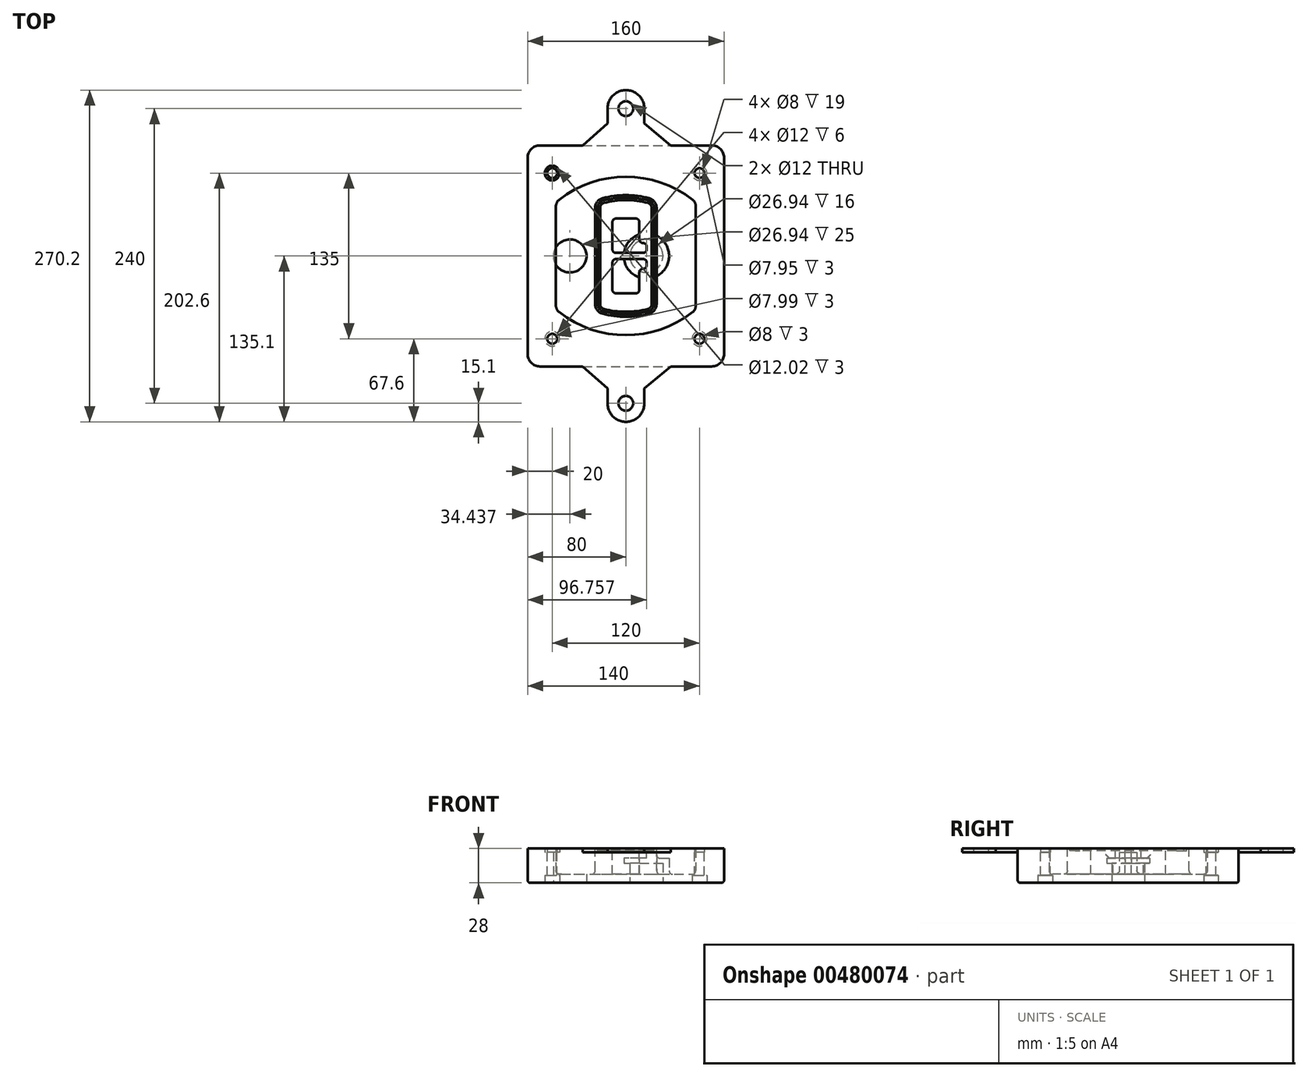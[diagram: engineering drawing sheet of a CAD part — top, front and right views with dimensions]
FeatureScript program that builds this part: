
annotation { "Feature Type Name" : "Feature", "Feature Type Description" : "" }
export const myFeature = defineFeature(function(context is Context, id is Id, definition is map)
    precondition{}
    {
        {
            var Q0;
            Q0=qCreatedBy(makeId("Top.planeOp"),FACE);
            var sketch = newSketch(context, id + "F0", { "sketchPlane" : qUnion([Q0])});
            skPoint(sketch, "E0.rect.middle", {"position": v(0, 0) * mm});
            skLineSegment(sketch, "E1.bottom", {"start": v(-70, -90) * mm, "end": v(70, -90) * mm});
            skLineSegment(sketch, "E1.top", {"start": v(-70, 90) * mm, "end": v(70, 90) * mm});
            skLineSegment(sketch, "E1.left", {"start": v(-80, -80) * mm, "end": v(-80, 80) * mm});
            skLineSegment(sketch, "E1.right", {"start": v(80, -80) * mm, "end": v(80, 80) * mm});
            skLineSegment(sketch, "E2", {"start": v(-80, 90) * mm, "end": v(80, -90) * mm, "construction": true});
            skLineSegment(sketch, "E3", {"start": v(80, 90) * mm, "end": v(-80, -90) * mm, "construction": true});
            skCircle(sketch, "E4", {"center": v(-60, 67.5) * mm, "radius": 4 * mm});
            skCircle(sketch, "E5", {"center": v(60, 67.5) * mm, "radius": 4 * mm});
            skCircle(sketch, "E6", {"center": v(60, -67.5) * mm, "radius": 4 * mm});
            skCircle(sketch, "E7", {"center": v(-60, -67.5) * mm, "radius": 4 * mm});
            skLineSegment(sketch, "E8", {"start": v(-60, 67.5) * mm, "end": v(60, 67.5) * mm, "construction": true});
            skLineSegment(sketch, "E9", {"start": v(60, 67.5) * mm, "end": v(60, -67.5) * mm, "construction": true});
            skLineSegment(sketch, "E10", {"start": v(60, -67.5) * mm, "end": v(-60, -67.5) * mm, "construction": true});
            skLineSegment(sketch, "E11", {"start": v(-60, -67.5) * mm, "end": v(-60, 67.5) * mm, "construction": true});
            skLineSegment(sketch, "E12", {"start": v(-60, 40.3) * mm, "end": v(-60, -40.3) * mm});
            skLineSegment(sketch, "E13", {"start": v(60, 40.3) * mm, "end": v(60, -40.3) * mm});
            skArc(sketch, "E14", {"start": v(56.15, 48.18) * mm, "mid": v(0, 67.5) * mm, "end": v(-56.15, 48.18) * mm});
            skArc(sketch, "E15", {"start": v(-56.15, -48.18) * mm, "mid": v(0, -67.5) * mm, "end": v(56.15, -48.18) * mm});
            skLineSegment(sketch, "E16", {"start": v(-60, 0) * mm, "end": v(60, 0) * mm, "construction": true});
            skPoint(sketch, "E17.visualSharp", {"position": v(-60, -45) * mm});
            skArc(sketch, "E17.filletArc", {"start": v(-60, -40.3) * mm, "mid": v(-58.99, -44.68) * mm, "end": v(-56.15, -48.18) * mm});
            skPoint(sketch, "E18.visualSharp", {"position": v(-60, 45) * mm});
            skArc(sketch, "E18.filletArc", {"start": v(-56.15, 48.18) * mm, "mid": v(-58.99, 44.68) * mm, "end": v(-60, 40.3) * mm});
            skPoint(sketch, "E19.visualSharp", {"position": v(60, 45) * mm});
            skArc(sketch, "E19.filletArc", {"start": v(60, 40.3) * mm, "mid": v(58.99, 44.68) * mm, "end": v(56.15, 48.18) * mm});
            skPoint(sketch, "E20.visualSharp", {"position": v(60, -45) * mm});
            skArc(sketch, "E20.filletArc", {"start": v(56.15, -48.18) * mm, "mid": v(58.99, -44.68) * mm, "end": v(60, -40.3) * mm});
            skPoint(sketch, "E21.visualSharp", {"position": v(-80, 90) * mm});
            skArc(sketch, "E21.filletArc", {"start": v(-70, 90) * mm, "mid": v(-77.07, 87.07) * mm, "end": v(-80, 80) * mm});
            skPoint(sketch, "E22.visualSharp", {"position": v(80, 90) * mm});
            skArc(sketch, "E22.filletArc", {"start": v(80, 80) * mm, "mid": v(77.07, 87.07) * mm, "end": v(70, 90) * mm});
            skPoint(sketch, "E23.visualSharp", {"position": v(80, -90) * mm});
            skArc(sketch, "E23.filletArc", {"start": v(70, -90) * mm, "mid": v(77.07, -87.07) * mm, "end": v(80, -80) * mm});
            skPoint(sketch, "E24.visualSharp", {"position": v(-80, -90) * mm});
            skArc(sketch, "E24.filletArc", {"start": v(-80, -80) * mm, "mid": v(-77.07, -87.07) * mm, "end": v(-70, -90) * mm});
            skArc(sketch, "E25.0", {"start": v(57, 40.3) * mm, "mid": v(56.3, 43.36) * mm, "end": v(54.3, 45.81) * mm});
            skLineSegment(sketch, "E25.1", {"start": v(57, 40.3) * mm, "end": v(57, -40.3) * mm});
            skArc(sketch, "E25.2", {"start": v(54.3, -45.81) * mm, "mid": v(56.3, -43.36) * mm, "end": v(57, -40.3) * mm});
            skArc(sketch, "E25.3", {"start": v(-54.3, -45.81) * mm, "mid": v(0, -64.5) * mm, "end": v(54.3, -45.81) * mm});
            skArc(sketch, "E25.4", {"start": v(-57, -40.3) * mm, "mid": v(-56.3, -43.36) * mm, "end": v(-54.3, -45.81) * mm});
            skArc(sketch, "E25.5", {"start": v(54.3, 45.81) * mm, "mid": v(0, 64.5) * mm, "end": v(-54.3, 45.81) * mm});
            skLineSegment(sketch, "E25.6", {"start": v(-57, 40.3) * mm, "end": v(-57, -40.3) * mm});
            skArc(sketch, "E25.7", {"start": v(-54.3, 45.81) * mm, "mid": v(-56.3, 43.36) * mm, "end": v(-57, 40.3) * mm});
            skArc(sketch, "E26.0", {"start": v(-58.62, 51.33) * mm, "mid": v(-62.58, 46.43) * mm, "end": v(-64, 40.3) * mm});
            skArc(sketch, "E26.1", {"start": v(58.62, 51.33) * mm, "mid": v(0, 71.5) * mm, "end": v(-58.62, 51.33) * mm});
            skArc(sketch, "E26.2", {"start": v(64, 40.3) * mm, "mid": v(62.58, 46.43) * mm, "end": v(58.62, 51.33) * mm});
            skLineSegment(sketch, "E26.3", {"start": v(64, 40.3) * mm, "end": v(64, -40.3) * mm});
            skArc(sketch, "E26.4", {"start": v(58.62, -51.33) * mm, "mid": v(62.58, -46.43) * mm, "end": v(64, -40.3) * mm});
            skLineSegment(sketch, "E26.5", {"start": v(-64, 40.3) * mm, "end": v(-64, -40.3) * mm});
            skArc(sketch, "E26.6", {"start": v(-58.62, -51.33) * mm, "mid": v(0, -71.5) * mm, "end": v(58.62, -51.33) * mm});
            skArc(sketch, "E26.7", {"start": v(-64, -40.3) * mm, "mid": v(-62.58, -46.43) * mm, "end": v(-58.62, -51.33) * mm});
            skSolve(sketch);
        }
        {
            var Q0;
            Q0=makeQuery(id+"F0.imprint","IMPRINT",FACE,{"disambiguationData":[TD([[makeQuery(id+"F0.imprint","IMPRINT",EDGE,{"derivedFrom":sQuery(id+"F0.wireOp",EDGE,"E1.bottom")}),1.0]])]});
            var Q1;
            Q1=makeQuery(id+"F0.imprint","IMPRINT",FACE,{"disambiguationData":[TD([[makeQuery(id+"F0.imprint","IMPRINT",EDGE,{"derivedFrom":sQuery(id+"F0.wireOp",EDGE,"E12")}),1.0]])]});
            var Q2;
            Q2=makeQuery(id+"F0.imprint","IMPRINT",FACE,{"disambiguationData":[TD([[makeQuery(id+"F0.imprint","IMPRINT",EDGE,{"derivedFrom":sQuery(id+"F0.wireOp",EDGE,"E25.0")}),1.0]])]});
            var Q3;
            Q3=makeQuery(id+"F0.imprint","IMPRINT",FACE,{"disambiguationData":[TD([[makeQuery(id+"F0.imprint","IMPRINT",EDGE,{"derivedFrom":sQuery(id+"F0.wireOp",EDGE,"E12")}),-1.0]])]});
            extrude(context, id + "F1", {"entities" : qUnion([Q0, Q1, Q2, Q3]), "oppositeDirection" : true, "depth" : 25 * mm});
        }
        {
            var Q0;
            Q0=makeQuery(id+"F0.imprint","IMPRINT",FACE,{"disambiguationData":[TD([[makeQuery(id+"F0.imprint","IMPRINT",EDGE,{"derivedFrom":sQuery(id+"F0.wireOp",EDGE,"E12")}),1.0]])]});
            extrude(context, id + "F2", {"entities" : qUnion([Q0]), "operationType" : NewBodyOperationType.ADD, "depth" : 3 * mm});
        }
        {
            var Q0;
            Q0=makeQuery(id+"F0.imprint","IMPRINT",FACE,{"disambiguationData":[TD([[makeQuery(id+"F0.imprint","IMPRINT",EDGE,{"derivedFrom":sQuery(id+"F0.wireOp",EDGE,"E25.0")}),1.0]])]});
            extrude(context, id + "F3", {"entities" : qUnion([Q0]), "operationType" : NewBodyOperationType.REMOVE, "oppositeDirection" : true, "depth" : 18 * mm});
        }
        {
            var Q0;
            Q0=makeQuery(id+"F2.opExtrude","CAP_FACE",FACE,{"disambiguationData":[OSD([sQuery(id+"F0.wireOp",EDGE,"E12"),sQuery(id+"F0.wireOp",EDGE,"E13"),sQuery(id+"F0.wireOp",EDGE,"E14"),sQuery(id+"F0.wireOp",EDGE,"E15"),sQuery(id+"F0.wireOp",EDGE,"E17.filletArc"),sQuery(id+"F0.wireOp",EDGE,"E18.filletArc"),sQuery(id+"F0.wireOp",EDGE,"E19.filletArc"),sQuery(id+"F0.wireOp",EDGE,"E20.filletArc"),sQuery(id+"F0.wireOp",EDGE,"E25.0"),sQuery(id+"F0.wireOp",EDGE,"E25.1"),sQuery(id+"F0.wireOp",EDGE,"E25.2"),sQuery(id+"F0.wireOp",EDGE,"E25.3"),sQuery(id+"F0.wireOp",EDGE,"E25.4"),sQuery(id+"F0.wireOp",EDGE,"E25.5"),sQuery(id+"F0.wireOp",EDGE,"E25.6"),sQuery(id+"F0.wireOp",EDGE,"E25.7")])],"isStart":false});
            var sketch = newSketch(context, id + "F4", { "sketchPlane" : qUnion([Q0])});
            skArc(sketch, "E27.0", {"start": v(-19.08, -46.97) * mm, "mid": v(0, -49.5) * mm, "end": v(19.08, -46.97) * mm});
            skArc(sketch, "E28.0", {"start": v(19.08, 46.97) * mm, "mid": v(0, 49.5) * mm, "end": v(-19.08, 46.97) * mm});
            skLineSegment(sketch, "E29", {"start": v(-25, 39.25) * mm, "end": v(-25, -39.25) * mm});
            skLineSegment(sketch, "E30", {"start": v(25, 39.25) * mm, "end": v(25, -39.25) * mm});
            skLineSegment(sketch, "E31", {"start": v(-25, 45.1) * mm, "end": v(25, 45.1) * mm, "construction": true});
            skLineSegment(sketch, "E32", {"start": v(-25, -45.1) * mm, "end": v(25, -45.1) * mm, "construction": true});
            skPoint(sketch, "E33.visualSharp", {"position": v(-25, 45.1) * mm});
            skArc(sketch, "E33.filletArc", {"start": v(-19.08, 46.97) * mm, "mid": v(-23.35, 44.11) * mm, "end": v(-25, 39.25) * mm});
            skPoint(sketch, "E34.visualSharp", {"position": v(25, 45.1) * mm});
            skArc(sketch, "E34.filletArc", {"start": v(25, 39.25) * mm, "mid": v(23.35, 44.11) * mm, "end": v(19.08, 46.97) * mm});
            skPoint(sketch, "E35.visualSharp", {"position": v(25, -45.1) * mm});
            skArc(sketch, "E35.filletArc", {"start": v(19.08, -46.97) * mm, "mid": v(23.35, -44.11) * mm, "end": v(25, -39.25) * mm});
            skPoint(sketch, "E36.visualSharp", {"position": v(-25, -45.1) * mm});
            skArc(sketch, "E36.filletArc", {"start": v(-25, -39.25) * mm, "mid": v(-23.35, -44.11) * mm, "end": v(-19.08, -46.97) * mm});
            skArc(sketch, "E37.0", {"start": v(54.3, 45.81) * mm, "mid": v(0, 64.5) * mm, "end": v(-54.3, 45.81) * mm});
            skArc(sketch, "E37.1", {"start": v(-54.3, 45.81) * mm, "mid": v(-56.3, 43.36) * mm, "end": v(-57, 40.3) * mm});
            skLineSegment(sketch, "E37.2", {"start": v(-57, 40.3) * mm, "end": v(-57, -40.3) * mm});
            skArc(sketch, "E37.3", {"start": v(-57, -40.3) * mm, "mid": v(-56.3, -43.36) * mm, "end": v(-54.3, -45.81) * mm});
            skArc(sketch, "E37.4", {"start": v(-54.3, -45.81) * mm, "mid": v(0, -64.5) * mm, "end": v(54.3, -45.81) * mm});
            skArc(sketch, "E37.5", {"start": v(54.3, -45.81) * mm, "mid": v(56.3, -43.36) * mm, "end": v(57, -40.3) * mm});
            skLineSegment(sketch, "E37.6", {"start": v(57, 40.3) * mm, "end": v(57, -40.3) * mm});
            skArc(sketch, "E37.7", {"start": v(57, 40.3) * mm, "mid": v(56.3, 43.36) * mm, "end": v(54.3, 45.81) * mm});
            skLineSegment(sketch, "E38.0", {"start": v(23, 39.25) * mm, "end": v(23, -39.25) * mm});
            skArc(sketch, "E38.1", {"start": v(18.56, -45.04) * mm, "mid": v(21.76, -42.9) * mm, "end": v(23, -39.25) * mm});
            skArc(sketch, "E38.2", {"start": v(-18.56, -45.04) * mm, "mid": v(0, -47.5) * mm, "end": v(18.56, -45.04) * mm});
            skArc(sketch, "E38.3", {"start": v(-23, -39.25) * mm, "mid": v(-21.76, -42.9) * mm, "end": v(-18.56, -45.04) * mm});
            skLineSegment(sketch, "E38.4", {"start": v(-23, 39.25) * mm, "end": v(-23, -39.25) * mm});
            skArc(sketch, "E38.5", {"start": v(23, 39.25) * mm, "mid": v(21.76, 42.9) * mm, "end": v(18.56, 45.04) * mm});
            skArc(sketch, "E38.6", {"start": v(-18.56, 45.04) * mm, "mid": v(-21.76, 42.9) * mm, "end": v(-23, 39.25) * mm});
            skArc(sketch, "E38.7", {"start": v(18.56, 45.04) * mm, "mid": v(0, 47.5) * mm, "end": v(-18.56, 45.04) * mm});
            skArc(sketch, "E39.0", {"start": v(21, 39.25) * mm, "mid": v(20.18, 41.68) * mm, "end": v(18.04, 43.1) * mm});
            skLineSegment(sketch, "E39.1", {"start": v(21, 39.25) * mm, "end": v(21, -39.25) * mm});
            skArc(sketch, "E39.2", {"start": v(18.04, -43.1) * mm, "mid": v(20.18, -41.68) * mm, "end": v(21, -39.25) * mm});
            skArc(sketch, "E39.3", {"start": v(-18.04, -43.1) * mm, "mid": v(0, -45.5) * mm, "end": v(18.04, -43.1) * mm});
            skArc(sketch, "E39.4", {"start": v(-21, -39.25) * mm, "mid": v(-20.18, -41.68) * mm, "end": v(-18.04, -43.1) * mm});
            skArc(sketch, "E39.5", {"start": v(18.04, 43.1) * mm, "mid": v(0, 45.5) * mm, "end": v(-18.04, 43.1) * mm});
            skLineSegment(sketch, "E39.6", {"start": v(-21, 39.25) * mm, "end": v(-21, -39.25) * mm});
            skArc(sketch, "E39.7", {"start": v(-18.04, 43.1) * mm, "mid": v(-20.18, 41.68) * mm, "end": v(-21, 39.25) * mm});
            skLineSegment(sketch, "E40", {"start": v(-25, 0) * mm, "end": v(25, 0) * mm, "construction": true});
            skLineSegment(sketch, "E41", {"start": v(-11, 5.5) * mm, "end": v(-11, 27.5) * mm});
            skLineSegment(sketch, "E42", {"start": v(-8, 30.5) * mm, "end": v(8, 30.5) * mm});
            skLineSegment(sketch, "E43", {"start": v(11, 27.5) * mm, "end": v(11, 13.5) * mm});
            skLineSegment(sketch, "E44", {"start": v(14, 10.5) * mm, "end": v(14, 10.5) * mm});
            skLineSegment(sketch, "E45", {"start": v(17, 7.5) * mm, "end": v(17, 5.5) * mm});
            skLineSegment(sketch, "E46", {"start": v(14, 2.5) * mm, "end": v(-8, 2.5) * mm});
            skPoint(sketch, "E47.visualSharp", {"position": v(-11, 30.5) * mm});
            skArc(sketch, "E47.filletArc", {"start": v(-8, 30.5) * mm, "mid": v(-10.12, 29.62) * mm, "end": v(-11, 27.5) * mm});
            skPoint(sketch, "E48.visualSharp", {"position": v(11, 30.5) * mm});
            skArc(sketch, "E48.filletArc", {"start": v(11, 27.5) * mm, "mid": v(10.12, 29.62) * mm, "end": v(8, 30.5) * mm});
            skPoint(sketch, "E49.visualSharp", {"position": v(11, 10.5) * mm});
            skArc(sketch, "E49.filletArc", {"start": v(11, 13.5) * mm, "mid": v(11.88, 11.38) * mm, "end": v(14, 10.5) * mm});
            skPoint(sketch, "E50.visualSharp", {"position": v(17, 10.5) * mm});
            skArc(sketch, "E50.filletArc", {"start": v(17, 7.5) * mm, "mid": v(16.12, 9.62) * mm, "end": v(14, 10.5) * mm});
            skPoint(sketch, "E51.visualSharp", {"position": v(17, 2.5) * mm});
            skArc(sketch, "E51.filletArc", {"start": v(14, 2.5) * mm, "mid": v(16.12, 3.38) * mm, "end": v(17, 5.5) * mm});
            skPoint(sketch, "E52.visualSharp", {"position": v(-11, 2.5) * mm});
            skArc(sketch, "E52.filletArc", {"start": v(-11, 5.5) * mm, "mid": v(-10.12, 3.38) * mm, "end": v(-8, 2.5) * mm});
            skLineSegment(sketch, "E53.0.MirrorCS", {"start": v(14, -2.5) * mm, "end": v(-8, -2.5) * mm});
            skArc(sketch, "E54.0.MirrorCS", {"start": v(-11, -5.5) * mm, "mid": v(-10.12, -3.38) * mm, "end": v(-8, -2.5) * mm});
            skLineSegment(sketch, "E55.0.MirrorCS", {"start": v(-11, -5.5) * mm, "end": v(-11, -27.5) * mm});
            skArc(sketch, "E56.0.MirrorCS", {"start": v(-8, -30.5) * mm, "mid": v(-10.12, -29.62) * mm, "end": v(-11, -27.5) * mm});
            skLineSegment(sketch, "E57.0.MirrorCS", {"start": v(-8, -30.5) * mm, "end": v(8, -30.5) * mm});
            skArc(sketch, "E58.0.MirrorCS", {"start": v(11, -27.5) * mm, "mid": v(10.12, -29.62) * mm, "end": v(8, -30.5) * mm});
            skLineSegment(sketch, "E59.0.MirrorCS", {"start": v(11, -27.5) * mm, "end": v(11, -13.5) * mm});
            skArc(sketch, "E60.0.MirrorCS", {"start": v(11, -13.5) * mm, "mid": v(11.88, -11.38) * mm, "end": v(14, -10.5) * mm});
            skArc(sketch, "E61.0.MirrorCS", {"start": v(17, -7.5) * mm, "mid": v(16.12, -9.62) * mm, "end": v(14, -10.5) * mm});
            skLineSegment(sketch, "E62.0.MirrorCS", {"start": v(17, -7.5) * mm, "end": v(17, -5.5) * mm});
            skArc(sketch, "E63.0.MirrorCS", {"start": v(14, -2.5) * mm, "mid": v(16.12, -3.38) * mm, "end": v(17, -5.5) * mm});
            skSolve(sketch);
        }
        {
            var Q0;
            Q0=makeQuery(id+"F4.imprint","IMPRINT",FACE,{"disambiguationData":[TD([[makeQuery(id+"F4.imprint","IMPRINT",EDGE,{"derivedFrom":sQuery(id+"F4.wireOp",EDGE,"E27.0")}),1.0]])]});
            var Q1;
            Q1=makeQuery(id+"F4.imprint","IMPRINT",FACE,{"disambiguationData":[TD([[makeQuery(id+"F4.imprint","IMPRINT",EDGE,{"derivedFrom":sQuery(id+"F4.wireOp",EDGE,"E38.0")}),-1.0]])]});
            var Q2;
            Q2=makeQuery(id+"F4.imprint","IMPRINT",FACE,{"disambiguationData":[TD([[makeQuery(id+"F4.imprint","IMPRINT",EDGE,{"derivedFrom":sQuery(id+"F4.wireOp",EDGE,"E39.0")}),1.0]])]});
            extrude(context, id + "F5", {"entities" : qUnion([Q0, Q1, Q2]), "operationType" : NewBodyOperationType.ADD, "endBound" : BoundingType.UP_TO_NEXT, "oppositeDirection" : true, "depth" : 25 * mm});
        }
        {
            var Q0;
            Q0=makeQuery(id+"F4.imprint","IMPRINT",FACE,{"disambiguationData":[TD([[makeQuery(id+"F4.imprint","IMPRINT",EDGE,{"derivedFrom":sQuery(id+"F4.wireOp",EDGE,"E38.0")}),-1.0]])]});
            extrude(context, id + "F6", {"entities" : qUnion([Q0]), "operationType" : NewBodyOperationType.REMOVE, "oppositeDirection" : true, "depth" : 2 * mm});
        }
        {
            var Q0;
            Q0=makeQuery(id+"F1.opExtrude","CAP_FACE",FACE,{"disambiguationData":[OSD([sQuery(id+"F0.wireOp",EDGE,"E1.bottom"),sQuery(id+"F0.wireOp",EDGE,"E1.top"),sQuery(id+"F0.wireOp",EDGE,"E1.left"),sQuery(id+"F0.wireOp",EDGE,"E1.right"),sQuery(id+"F0.wireOp",EDGE,"E4"),sQuery(id+"F0.wireOp",EDGE,"E5"),sQuery(id+"F0.wireOp",EDGE,"E6"),sQuery(id+"F0.wireOp",EDGE,"E7"),sQuery(id+"F0.wireOp",EDGE,"E21.filletArc"),sQuery(id+"F0.wireOp",EDGE,"E22.filletArc"),sQuery(id+"F0.wireOp",EDGE,"E23.filletArc"),sQuery(id+"F0.wireOp",EDGE,"E24.filletArc")])],"isStart":false});
            var sketch = newSketch(context, id + "F7", { "sketchPlane" : qUnion([Q0])});
            skCircle(sketch, "E64", {"center": v(16.76, 0) * mm, "radius": 13.47 * mm});
            skCircle(sketch, "E65", {"center": v(-45.56, 0) * mm, "radius": 13.47 * mm});
            skLineSegment(sketch, "E66", {"start": v(80, 0) * mm, "end": v(-80, 0) * mm});
            skCircle(sketch, "E67", {"center": v(16.76, 0) * mm, "radius": 18.47 * mm});
            skCircle(sketch, "E68", {"center": v(60, -67.5) * mm, "radius": 6 * mm});
            skCircle(sketch, "E69", {"center": v(-60, -67.5) * mm, "radius": 6 * mm});
            skCircle(sketch, "E70", {"center": v(-60, 67.5) * mm, "radius": 6 * mm});
            skCircle(sketch, "E71", {"center": v(60, 67.5) * mm, "radius": 6 * mm});
            skSolve(sketch);
        }
        {
            var Q0;
            {var subQ1=sQuery(id+"F7.wireOp",EDGE,"E66");var subQ4=sQuery(id+"F7.wireOp",EDGE,"E64");var subQ6=makeQuery(id+"F7.imprint","INTERSECT",VERTEX,{"disambiguationData":[OD(0.0)],"derivedFrom":[subQ4,subQ1]});Q0=makeQuery(id+"F7.imprint","IMPRINT",FACE,{"disambiguationData":[TD([[makeQuery(id+"F7.imprint","IMPRINT",EDGE,{"disambiguationData":[TD([[subQ6,-1.0]])],"derivedFrom":subQ4}),-1.0]])]});}
            var Q1;
            {var subQ0=sQuery(id+"F7.wireOp",EDGE,"E66");var subQ1=sQuery(id+"F7.wireOp",EDGE,"E64");var subQ3=makeQuery(id+"F7.imprint","INTERSECT",VERTEX,{"disambiguationData":[OD(0.0)],"derivedFrom":[subQ1,subQ0]});Q1=makeQuery(id+"F7.imprint","IMPRINT",FACE,{"disambiguationData":[TD([[makeQuery(id+"F7.imprint","IMPRINT",EDGE,{"disambiguationData":[TD([[subQ3,-1.0]])],"derivedFrom":subQ1}),1.0]])]});}
            var Q2;
            {var subQ0=sQuery(id+"F7.wireOp",EDGE,"E66");var subQ1=sQuery(id+"F7.wireOp",EDGE,"E64");var subQ3=makeQuery(id+"F7.imprint","INTERSECT",VERTEX,{"disambiguationData":[OD(0.0)],"derivedFrom":[subQ1,subQ0]});Q2=makeQuery(id+"F7.imprint","IMPRINT",FACE,{"disambiguationData":[TD([[makeQuery(id+"F7.imprint","IMPRINT",EDGE,{"disambiguationData":[TD([[subQ3,1.0]])],"derivedFrom":subQ1}),1.0]])]});}
            var Q3;
            {var subQ1=sQuery(id+"F7.wireOp",EDGE,"E66");var subQ4=sQuery(id+"F7.wireOp",EDGE,"E64");var subQ6=makeQuery(id+"F7.imprint","INTERSECT",VERTEX,{"disambiguationData":[OD(0.0)],"derivedFrom":[subQ4,subQ1]});Q3=makeQuery(id+"F7.imprint","IMPRINT",FACE,{"disambiguationData":[TD([[makeQuery(id+"F7.imprint","IMPRINT",EDGE,{"disambiguationData":[TD([[subQ6,1.0]])],"derivedFrom":subQ4}),-1.0]])]});}
            extrude(context, id + "F8", {"entities" : qUnion([Q0, Q1, Q2, Q3]), "operationType" : NewBodyOperationType.ADD, "oppositeDirection" : true, "depth" : 20 * mm});
        }
        {
            var Q0;
            {var subQ0=sQuery(id+"F7.wireOp",EDGE,"E66");var subQ1=sQuery(id+"F7.wireOp",EDGE,"E64");var subQ3=makeQuery(id+"F7.imprint","INTERSECT",VERTEX,{"disambiguationData":[OD(0.0)],"derivedFrom":[subQ1,subQ0]});Q0=makeQuery(id+"F7.imprint","IMPRINT",FACE,{"disambiguationData":[TD([[makeQuery(id+"F7.imprint","IMPRINT",EDGE,{"disambiguationData":[TD([[subQ3,-1.0]])],"derivedFrom":subQ1}),1.0]])]});}
            var Q1;
            {var subQ0=sQuery(id+"F7.wireOp",EDGE,"E66");var subQ1=sQuery(id+"F7.wireOp",EDGE,"E64");var subQ3=makeQuery(id+"F7.imprint","INTERSECT",VERTEX,{"disambiguationData":[OD(0.0)],"derivedFrom":[subQ1,subQ0]});Q1=makeQuery(id+"F7.imprint","IMPRINT",FACE,{"disambiguationData":[TD([[makeQuery(id+"F7.imprint","IMPRINT",EDGE,{"disambiguationData":[TD([[subQ3,1.0]])],"derivedFrom":subQ1}),1.0]])]});}
            extrude(context, id + "F9", {"entities" : qUnion([Q0, Q1]), "operationType" : NewBodyOperationType.REMOVE, "oppositeDirection" : true, "depth" : 16 * mm});
        }
        {
            var Q0;
            {var subQ0=sQuery(id+"F7.wireOp",EDGE,"E66");var subQ1=sQuery(id+"F7.wireOp",EDGE,"E65");var subQ3=makeQuery(id+"F7.imprint","INTERSECT",VERTEX,{"disambiguationData":[OD(0.0)],"derivedFrom":[subQ1,subQ0]});Q0=makeQuery(id+"F7.imprint","IMPRINT",FACE,{"disambiguationData":[TD([[makeQuery(id+"F7.imprint","IMPRINT",EDGE,{"disambiguationData":[TD([[subQ3,-1.0]])],"derivedFrom":subQ1}),1.0]])]});}
            var Q1;
            {var subQ0=sQuery(id+"F7.wireOp",EDGE,"E66");var subQ1=sQuery(id+"F7.wireOp",EDGE,"E65");var subQ3=makeQuery(id+"F7.imprint","INTERSECT",VERTEX,{"disambiguationData":[OD(0.0)],"derivedFrom":[subQ1,subQ0]});Q1=makeQuery(id+"F7.imprint","IMPRINT",FACE,{"disambiguationData":[TD([[makeQuery(id+"F7.imprint","IMPRINT",EDGE,{"disambiguationData":[TD([[subQ3,1.0]])],"derivedFrom":subQ1}),1.0]])]});}
            extrude(context, id + "F10", {"entities" : qUnion([Q0, Q1]), "operationType" : NewBodyOperationType.REMOVE, "oppositeDirection" : true, "depth" : 25 * mm});
        }
        {
            var Q0;
            Q0=makeQuery(id+"F7.imprint","IMPRINT",FACE,{"disambiguationData":[TD([[makeQuery(id+"F7.imprint","IMPRINT",EDGE,{"derivedFrom":sQuery(id+"F7.wireOp",EDGE,"E68")}),1.0]])]});
            var Q1;
            Q1=makeQuery(id+"F7.imprint","IMPRINT",FACE,{"disambiguationData":[TD([[makeQuery(id+"F7.imprint","IMPRINT",EDGE,{"derivedFrom":makeQuery(id+"F1.opExtrude","CAP_EDGE",EDGE,{"disambiguationData":[OSD([sQuery(id+"F0.wireOp",EDGE,"E5")])],"isStart":false})}),-1.0]])]});
            var Q2;
            Q2=makeQuery(id+"F7.imprint","IMPRINT",FACE,{"disambiguationData":[TD([[makeQuery(id+"F7.imprint","IMPRINT",EDGE,{"derivedFrom":sQuery(id+"F7.wireOp",EDGE,"E69")}),1.0]])]});
            var Q3;
            Q3=makeQuery(id+"F7.imprint","IMPRINT",FACE,{"disambiguationData":[TD([[makeQuery(id+"F7.imprint","IMPRINT",EDGE,{"derivedFrom":makeQuery(id+"F1.opExtrude","CAP_EDGE",EDGE,{"disambiguationData":[OSD([sQuery(id+"F0.wireOp",EDGE,"E4")])],"isStart":false})}),-1.0]])]});
            var Q4;
            Q4=makeQuery(id+"F7.imprint","IMPRINT",FACE,{"disambiguationData":[TD([[makeQuery(id+"F7.imprint","IMPRINT",EDGE,{"derivedFrom":sQuery(id+"F7.wireOp",EDGE,"E70")}),1.0]])]});
            var Q5;
            Q5=makeQuery(id+"F7.imprint","IMPRINT",FACE,{"disambiguationData":[TD([[makeQuery(id+"F7.imprint","IMPRINT",EDGE,{"derivedFrom":makeQuery(id+"F1.opExtrude","CAP_EDGE",EDGE,{"disambiguationData":[OSD([sQuery(id+"F0.wireOp",EDGE,"E7")])],"isStart":false})}),-1.0]])]});
            var Q6;
            Q6=makeQuery(id+"F7.imprint","IMPRINT",FACE,{"disambiguationData":[TD([[makeQuery(id+"F7.imprint","IMPRINT",EDGE,{"derivedFrom":sQuery(id+"F7.wireOp",EDGE,"E71")}),1.0]])]});
            var Q7;
            Q7=makeQuery(id+"F7.imprint","IMPRINT",FACE,{"disambiguationData":[TD([[makeQuery(id+"F7.imprint","IMPRINT",EDGE,{"derivedFrom":makeQuery(id+"F1.opExtrude","CAP_EDGE",EDGE,{"disambiguationData":[OSD([sQuery(id+"F0.wireOp",EDGE,"E6")])],"isStart":false})}),-1.0]])]});
            extrude(context, id + "F11", {"entities" : qUnion([Q0, Q1, Q2, Q3, Q4, Q5, Q6, Q7]), "operationType" : NewBodyOperationType.REMOVE, "oppositeDirection" : true, "depth" : 6 * mm});
        }
        {
            var Q0;
            Q0=makeQuery(id+"F9.boolean.opBoolean","COPY",FACE,{"derivedFrom":makeQuery(id+"F9.opExtrude","CAP_FACE",FACE,{"disambiguationData":[OSD([sQuery(id+"F7.wireOp",EDGE,"E64")])],"isStart":false})});
            var sketch = newSketch(context, id + "F12", { "sketchPlane" : qUnion([Q0])});
            skArc(sketch, "E72.0", {"start": v(11, 17.55) * mm, "mid": v(2.57, 11.82) * mm, "end": v(-1.54, 2.5) * mm});
            skArc(sketch, "E72.1", {"start": v(-1.54, -2.5) * mm, "mid": v(2.57, -11.82) * mm, "end": v(11, -17.55) * mm});
            skLineSegment(sketch, "E73", {"start": v(-1.54, -2.5) * mm, "end": v(14, -2.5) * mm});
            skLineSegment(sketch, "E74.0", {"start": v(14, 2.5) * mm, "end": v(-1.54, 2.5) * mm});
            skArc(sketch, "E74.1", {"start": v(14, 2.5) * mm, "mid": v(16.12, 3.38) * mm, "end": v(17, 5.5) * mm});
            skLineSegment(sketch, "E74.2", {"start": v(17, 7.5) * mm, "end": v(17, 5.5) * mm});
            skArc(sketch, "E74.3", {"start": v(17, 7.5) * mm, "mid": v(16.12, 9.62) * mm, "end": v(14, 10.5) * mm});
            skArc(sketch, "E74.4", {"start": v(11, 13.5) * mm, "mid": v(11.88, 11.38) * mm, "end": v(14, 10.5) * mm});
            skLineSegment(sketch, "E74.5", {"start": v(11, 17.55) * mm, "end": v(11, 13.5) * mm});
            skLineSegment(sketch, "E74.7", {"start": v(14, -2.5) * mm, "end": v(-1.54, -2.5) * mm});
            skArc(sketch, "E74.8", {"start": v(14, -2.5) * mm, "mid": v(16.12, -3.38) * mm, "end": v(17, -5.5) * mm});
            skLineSegment(sketch, "E74.9", {"start": v(17, -7.5) * mm, "end": v(17, -5.5) * mm});
            skArc(sketch, "E74.10", {"start": v(17, -7.5) * mm, "mid": v(16.12, -9.62) * mm, "end": v(14, -10.5) * mm});
            skArc(sketch, "E74.11", {"start": v(11, -13.5) * mm, "mid": v(11.88, -11.38) * mm, "end": v(14, -10.5) * mm});
            skLineSegment(sketch, "E74.12", {"start": v(11, -17.55) * mm, "end": v(11, -13.5) * mm});
            skPoint(sketch, "E75.orphan", {"position": v(11, -27.5) * mm});
            skPoint(sketch, "E76.orphan", {"position": v(-8, -2.5) * mm});
            skPoint(sketch, "E77.orphan", {"position": v(-8, 2.5) * mm});
            skPoint(sketch, "E78.orphan", {"position": v(11, 27.5) * mm});
            skSolve(sketch);
        }
        {
            var Q0;
            {var subQ7=sQuery(id+"F12.wireOp",EDGE,"E72.0");var subQ14=sQuery(id+"F12.wireOp",EDGE,"E72.1");var subQ16=sQuery(id+"F12.wireOp",EDGE,"E74.1");var subQ18=sQuery(id+"F12.wireOp",EDGE,"E74.8");Q0=qUnion([makeQuery(id+"F12.imprint","IMPRINT",FACE,{"disambiguationData":[TD([[makeQuery(id+"F12.imprint","IMPRINT",EDGE,{"derivedFrom":subQ7}),1.0]])]}),makeQuery(id+"F12.imprint","IMPRINT",FACE,{"disambiguationData":[TD([[makeQuery(id+"F12.imprint","IMPRINT",EDGE,{"derivedFrom":subQ14}),1.0]])]}),makeQuery(id+"F12.imprint","IMPRINT",FACE,{"disambiguationData":[TD([[makeQuery(id+"F12.imprint","IMPRINT",EDGE,{"derivedFrom":subQ16}),1.0]])]}),makeQuery(id+"F12.imprint","IMPRINT",FACE,{"disambiguationData":[TD([[makeQuery(id+"F12.imprint","IMPRINT",EDGE,{"derivedFrom":subQ18}),-1.0]])]})]);}
            var Q1;
            Q1=makeQuery(id+"F5.boolean.opBoolean","SPLIT",FACE,{"disambiguationData":[TD([makeQuery(id+"F5.opExtrude","SWEPT_FACE",FACE,{"disambiguationData":[OSD([sQuery(id+"F4.wireOp",EDGE,"E41")])]})])],"derivedFrom":makeQuery(id+"F3.boolean.opBoolean","COPY",FACE,{"derivedFrom":makeQuery(id+"F3.opExtrude","CAP_FACE",FACE,{"disambiguationData":[OSD([sQuery(id+"F0.wireOp",EDGE,"E25.0"),sQuery(id+"F0.wireOp",EDGE,"E25.1"),sQuery(id+"F0.wireOp",EDGE,"E25.2"),sQuery(id+"F0.wireOp",EDGE,"E25.3"),sQuery(id+"F0.wireOp",EDGE,"E25.4"),sQuery(id+"F0.wireOp",EDGE,"E25.5"),sQuery(id+"F0.wireOp",EDGE,"E25.6"),sQuery(id+"F0.wireOp",EDGE,"E25.7")])],"isStart":false})})});
            extrude(context, id + "F13", {"entities" : qUnion([Q0]), "operationType" : NewBodyOperationType.REMOVE, "endBound" : BoundingType.UP_TO_SURFACE, "endBoundEntityFace" : qUnion([Q1]), "depth" : 25 * mm});
        }
        {
            var Q0;
            Q0=makeQuery(id+"F3.boolean.opBoolean","COPY",EDGE,{"derivedFrom":makeQuery(id+"F3.opExtrude","CAP_EDGE",EDGE,{"disambiguationData":[OSD([sQuery(id+"F0.wireOp",EDGE,"E25.6")])],"isStart":false})});
            var Q1;
            Q1=makeQuery(id+"F8.boolean.opBoolean","INTERSECT",EDGE,{"derivedFrom":[makeQuery(id+"F5.opExtrude","SWEPT_FACE",FACE,{"disambiguationData":[OSD([sQuery(id+"F4.wireOp",EDGE,"E30")])]}),makeQuery(id+"F8.opExtrude","CAP_FACE",FACE,{"disambiguationData":[OSD([sQuery(id+"F7.wireOp",EDGE,"E67")])],"isStart":false})]});
            var Q2;
            Q2=makeQuery(id+"F8.boolean.opBoolean","INTERSECT",EDGE,{"disambiguationData":[OD(1.0)],"derivedFrom":[makeQuery(id+"F5.opExtrude","SWEPT_FACE",FACE,{"disambiguationData":[OSD([sQuery(id+"F4.wireOp",EDGE,"E30")])]}),makeQuery(id+"F8.opExtrude","SWEPT_FACE",FACE,{"disambiguationData":[OSD([sQuery(id+"F7.wireOp",EDGE,"E67")])]})]});
            var Q3;
            {var subQ0=sQuery(id+"F4.wireOp",EDGE,"E30");Q3=makeQuery(id+"F8.boolean.opBoolean","SPLIT",EDGE,{"disambiguationData":[TD([makeQuery(id+"F5.opExtrude","SWEPT_FACE",FACE,{"disambiguationData":[OSD([sQuery(id+"F4.wireOp",EDGE,"E35.filletArc")])]})])],"derivedFrom":makeQuery(id+"F5.opExtrude","CAP_EDGE",EDGE,{"disambiguationData":[OSD([subQ0])],"isStart":false})});}
            var Q4;
            {var subQ0=sQuery(id+"F0.wireOp",EDGE,"E25.7");var subQ1=sQuery(id+"F0.wireOp",EDGE,"E25.1");var subQ2=sQuery(id+"F0.wireOp",EDGE,"E25.6");var subQ3=sQuery(id+"F0.wireOp",EDGE,"E25.5");var subQ4=sQuery(id+"F0.wireOp",EDGE,"E25.4");var subQ5=sQuery(id+"F0.wireOp",EDGE,"E25.0");var subQ6=sQuery(id+"F0.wireOp",EDGE,"E25.2");var subQ7=sQuery(id+"F0.wireOp",EDGE,"E25.3");Q4=makeQuery(id+"F8.boolean.opBoolean","INTERSECT",EDGE,{"derivedFrom":[makeQuery(id+"F5.boolean.opBoolean","SPLIT",FACE,{"disambiguationData":[TD([makeQuery(id+"F2.opExtrude","SWEPT_FACE",FACE,{"disambiguationData":[OSD([subQ5])]})])],"derivedFrom":makeQuery(id+"F3.boolean.opBoolean","COPY",FACE,{"derivedFrom":makeQuery(id+"F3.opExtrude","CAP_FACE",FACE,{"disambiguationData":[OSD([subQ5,subQ1,subQ6,subQ7,subQ4,subQ3,subQ2,subQ0])],"isStart":false})})}),makeQuery(id+"F8.opExtrude","SWEPT_FACE",FACE,{"disambiguationData":[OSD([sQuery(id+"F7.wireOp",EDGE,"E67")])]})]});}
            var Q5;
            Q5=makeQuery(id+"F8.boolean.opBoolean","INTERSECT",EDGE,{"disambiguationData":[OD(0.0)],"derivedFrom":[makeQuery(id+"F5.opExtrude","SWEPT_FACE",FACE,{"disambiguationData":[OSD([sQuery(id+"F4.wireOp",EDGE,"E30")])]}),makeQuery(id+"F8.opExtrude","SWEPT_FACE",FACE,{"disambiguationData":[OSD([sQuery(id+"F7.wireOp",EDGE,"E67")])]})]});
            fillet(context, id + "F14", {"entities" : qUnion([Q0, Q1, Q2, Q3, Q4, Q5]), "radius" : 3 * mm, "tangentPropagation" : true, "allowEdgeOverflow" : false});
        }
        {
            var Q0;
            Q0=makeQuery(id+"F1.opExtrude","CAP_EDGE",EDGE,{"disambiguationData":[OSD([sQuery(id+"F0.wireOp",EDGE,"E1.bottom")])],"isStart":false});
            fillet(context, id + "F15", {"entities" : qUnion([Q0]), "radius" : 2 * mm, "tangentPropagation" : true, "allowEdgeOverflow" : false});
        }
        {
            var Q0;
            {var subQ0=sQuery(id+"F0.wireOp",EDGE,"E21.filletArc");var subQ1=sQuery(id+"F0.wireOp",EDGE,"E7");var subQ2=sQuery(id+"F0.wireOp",EDGE,"E6");var subQ3=sQuery(id+"F0.wireOp",EDGE,"E5");var subQ4=sQuery(id+"F0.wireOp",EDGE,"E4");var subQ5=sQuery(id+"F0.wireOp",EDGE,"E22.filletArc");var subQ6=sQuery(id+"F0.wireOp",EDGE,"E1.bottom");var subQ7=sQuery(id+"F0.wireOp",EDGE,"E1.right");var subQ8=sQuery(id+"F0.wireOp",EDGE,"E1.top");var subQ9=sQuery(id+"F0.wireOp",EDGE,"E1.left");var subQ10=sQuery(id+"F0.wireOp",EDGE,"E23.filletArc");var subQ11=sQuery(id+"F0.wireOp",EDGE,"E24.filletArc");Q0=makeQuery(id+"F2.boolean.opBoolean","SPLIT",FACE,{"disambiguationData":[TD([makeQuery(id+"F1.opExtrude","SWEPT_FACE",FACE,{"disambiguationData":[OSD([subQ6])]})])],"derivedFrom":makeQuery(id+"F1.opExtrude","CAP_FACE",FACE,{"disambiguationData":[OSD([subQ6,subQ8,subQ9,subQ7,subQ4,subQ3,subQ2,subQ1,subQ0,subQ5,subQ10,subQ11])],"isStart":true})});}
            var sketch = newSketch(context, id + "F16", { "sketchPlane" : qUnion([Q0])});
            skLineSegment(sketch, "E79", {"start": v(-70, 90) * mm, "end": v(70, 90) * mm});
            skLineSegment(sketch, "E80", {"start": v(-80, 80) * mm, "end": v(-80, -80) * mm});
            skLineSegment(sketch, "E81", {"start": v(-70, -90) * mm, "end": v(70, -90) * mm});
            skLineSegment(sketch, "E82", {"start": v(80, -80) * mm, "end": v(80, 80) * mm});
            skCircle(sketch, "E83", {"center": v(60, 67.5) * mm, "radius": 3.98 * mm});
            skCircle(sketch, "E84", {"center": v(-60, 67.5) * mm, "radius": 6 * mm});
            skCircle(sketch, "E85", {"center": v(-60, -67.5) * mm, "radius": 4 * mm});
            skCircle(sketch, "E86", {"center": v(60, -67.5) * mm, "radius": 4 * mm});
            skLineSegment(sketch, "E87", {"start": v(0, 90) * mm, "end": v(0, 120) * mm, "construction": true});
            skCircle(sketch, "E88", {"center": v(0, 120) * mm, "radius": 6 * mm});
            skArc(sketch, "E89", {"start": v(15.06, 120) * mm, "mid": v(0.06, 135.1) * mm, "end": v(-14.94, 120) * mm});
            skLineSegment(sketch, "E90", {"start": v(-14.94, 120) * mm, "end": v(-14.86, 108) * mm});
            skLineSegment(sketch, "E91", {"start": v(15.06, 120) * mm, "end": v(15.06, 108) * mm});
            skLineSegment(sketch, "E92", {"start": v(-14.86, 108) * mm, "end": v(-35.13, 90) * mm});
            skLineSegment(sketch, "E93", {"start": v(15.06, 108) * mm, "end": v(36.48, 90) * mm});
            skArc(sketch, "E94.1", {"start": v(-70, 90) * mm, "mid": v(-77.07, 87.07) * mm, "end": v(-80, 80) * mm});
            skArc(sketch, "E94.3", {"start": v(80, 80) * mm, "mid": v(77.07, 87.07) * mm, "end": v(70, 90) * mm});
            skArc(sketch, "E94.5", {"start": v(70, -90) * mm, "mid": v(77.07, -87.07) * mm, "end": v(80, -80) * mm});
            skArc(sketch, "E94.7", {"start": v(-80, -80) * mm, "mid": v(-77.07, -87.07) * mm, "end": v(-70, -90) * mm});
            skArc(sketch, "E94.12", {"start": v(-56.15, -48.18) * mm, "mid": v(0, -67.5) * mm, "end": v(56.15, -48.18) * mm});
            skArc(sketch, "E94.13", {"start": v(56.15, -48.18) * mm, "mid": v(58.99, -44.68) * mm, "end": v(60, -40.3) * mm});
            skLineSegment(sketch, "E94.14", {"start": v(60, 40.3) * mm, "end": v(60, -40.3) * mm});
            skArc(sketch, "E94.15", {"start": v(-60, -40.3) * mm, "mid": v(-58.99, -44.68) * mm, "end": v(-56.15, -48.18) * mm});
            skLineSegment(sketch, "E94.16", {"start": v(-60, 40.3) * mm, "end": v(-60, -40.3) * mm});
            skArc(sketch, "E94.17", {"start": v(-56.15, 48.18) * mm, "mid": v(-58.99, 44.68) * mm, "end": v(-60, 40.3) * mm});
            skArc(sketch, "E94.18", {"start": v(56.15, 48.18) * mm, "mid": v(0, 67.5) * mm, "end": v(-56.15, 48.18) * mm});
            skArc(sketch, "E94.19", {"start": v(60, 40.3) * mm, "mid": v(58.99, 44.68) * mm, "end": v(56.15, 48.18) * mm});
            skLineSegment(sketch, "E95", {"start": v(0, -90) * mm, "end": v(0, -120) * mm, "construction": true});
            skPoint(sketch, "E95.endSnap0", {"position": v(0, -90) * mm});
            skLineSegment(sketch, "E96", {"start": v(-80, 0) * mm, "end": v(80, 0) * mm, "construction": true});
            skLineSegment(sketch, "E97.MirrorCS", {"start": v(15.06, -108) * mm, "end": v(36.48, -90) * mm});
            skLineSegment(sketch, "E98.MirrorCS", {"start": v(-14.86, -108) * mm, "end": v(-35.13, -90) * mm});
            skLineSegment(sketch, "E99.MirrorCS", {"start": v(15.06, -120) * mm, "end": v(15.06, -108) * mm});
            skLineSegment(sketch, "E100.MirrorCS", {"start": v(-14.94, -120) * mm, "end": v(-14.86, -108) * mm});
            skCircle(sketch, "E101.MirrorC", {"center": v(0, -120) * mm, "radius": 6 * mm});
            skArc(sketch, "E102.MirrorCS", {"start": v(15.06, -120) * mm, "mid": v(0.06, -135.1) * mm, "end": v(-14.94, -120) * mm});
            skSolve(sketch);
        }
        {
            var Q0;
            Q0 = qSketchRegion(id + "F16", true);
            var Q1;
            Q1=makeQuery(id+"F2.opExtrude","CAP_FACE",FACE,{"disambiguationData":[OSD([sQuery(id+"F0.wireOp",EDGE,"E12"),sQuery(id+"F0.wireOp",EDGE,"E13"),sQuery(id+"F0.wireOp",EDGE,"E14"),sQuery(id+"F0.wireOp",EDGE,"E15"),sQuery(id+"F0.wireOp",EDGE,"E17.filletArc"),sQuery(id+"F0.wireOp",EDGE,"E18.filletArc"),sQuery(id+"F0.wireOp",EDGE,"E19.filletArc"),sQuery(id+"F0.wireOp",EDGE,"E20.filletArc"),sQuery(id+"F0.wireOp",EDGE,"E25.0"),sQuery(id+"F0.wireOp",EDGE,"E25.1"),sQuery(id+"F0.wireOp",EDGE,"E25.2"),sQuery(id+"F0.wireOp",EDGE,"E25.3"),sQuery(id+"F0.wireOp",EDGE,"E25.4"),sQuery(id+"F0.wireOp",EDGE,"E25.5"),sQuery(id+"F0.wireOp",EDGE,"E25.6"),sQuery(id+"F0.wireOp",EDGE,"E25.7")])],"isStart":false});
            extrude(context, id + "F17", {"entities" : qUnion([Q0]), "operationType" : NewBodyOperationType.ADD, "endBound" : BoundingType.UP_TO_SURFACE, "endBoundEntityFace" : qUnion([Q1]), "depth" : 25 * mm});
        }
    });
